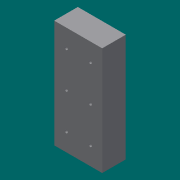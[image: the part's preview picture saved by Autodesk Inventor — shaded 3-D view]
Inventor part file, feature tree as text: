
AUTODESK INVENTOR PART (.ipt)
format: ipt  version: 2013 (Build 170138000, 138)  size: 89,088 bytes
history: native  units: mm
features: other x1, extrude x1, sketch x1
ambient origin geometry x8: Origin, YZ Plane, XZ Plane, XY Plane, X Axis, Y Axis, Z Axis, Center Point
feature tree (3):
  other  "ソリッド1"
  extrude  "押し出し1"  Depth=40.0mm
  sketch  "スケッチ1"
